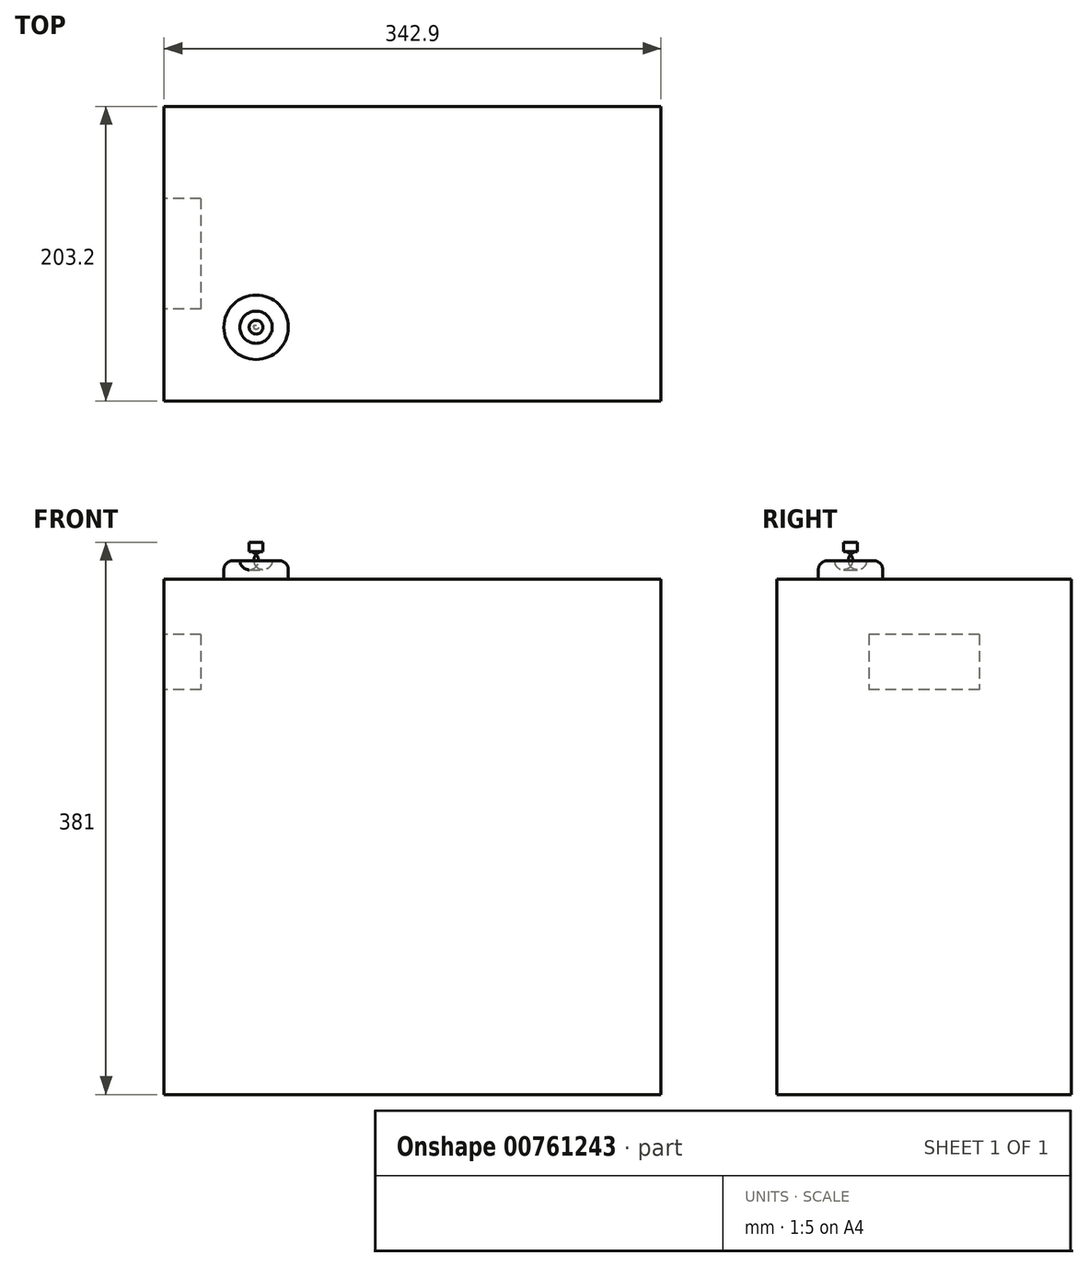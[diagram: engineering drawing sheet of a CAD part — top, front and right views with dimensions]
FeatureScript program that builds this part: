
annotation { "Feature Type Name" : "Feature", "Feature Type Description" : "" }
export const myFeature = defineFeature(function(context is Context, id is Id, definition is map)
    precondition{}
    {
        {
            var Q0;
            Q0=qCreatedBy(makeId("Top.planeOp"),FACE);
            var sketch = newSketch(context, id + "F0", { "sketchPlane" : qUnion([Q0])});
            skLineSegment(sketch, "E0.bottom", {"start": v(0, 203.2) * mm, "end": v(342.9, 203.2) * mm});
            skLineSegment(sketch, "E0.top", {"start": v(0, 0) * mm, "end": v(342.9, 0) * mm});
            skLineSegment(sketch, "E0.left", {"start": v(0, 203.2) * mm, "end": v(0, 0) * mm});
            skLineSegment(sketch, "E0.right", {"start": v(342.9, 203.2) * mm, "end": v(342.9, 0) * mm});
            skSolve(sketch);
        }
        {
            var Q0;
            Q0 = qSketchRegion(id + "F0", true);
            extrude(context, id + "F1", {"entities" : qUnion([Q0]), "depth" : 355.6 * mm, "offsetDistance" : 25 * mm});
        }
        {
            var Q0;
            Q0=makeQuery(id+"F1.opExtrude","SWEPT_FACE",FACE,{"disambiguationData":[OSD([sQuery(id+"F0.wireOp",EDGE,"E0.top")])]});
            cPlane(context, id + "F2", {"entities" : qUnion([Q0]), "cplaneType" : CPlaneType.OFFSET, "offset" : 50.8 * mm, "oppositeDirection" : true, "width" : 150 * mm, "height" : 150 * mm});
        }
        {
            var Q0;
            Q0=qCreatedBy(id+"F2.planeOp",FACE);
            var sketch = newSketch(context, id + "F3", { "sketchPlane" : qUnion([Q0])});
            skLineSegment(sketch, "E1", {"start": v(63.5, 323.9) * mm, "end": v(63.5, 400.93) * mm, "construction": true});
            skLineSegment(sketch, "E2", {"start": v(63.5, 355.6) * mm, "end": v(85.72, 355.6) * mm});
            skLineSegment(sketch, "E3", {"start": v(85.72, 355.6) * mm, "end": v(85.72, 361.95) * mm});
            skArc(sketch, "E4", {"start": v(85.72, 361.95) * mm, "mid": v(83.87, 366.44) * mm, "end": v(79.38, 368.3) * mm});
            skLineSegment(sketch, "E5", {"start": v(79.38, 368.3) * mm, "end": v(74.61, 368.3) * mm});
            skLineSegment(sketch, "E6", {"start": v(63.5, 381) * mm, "end": v(63.5, 355.6) * mm});
            skArc(sketch, "E7", {"start": v(74.61, 368.3) * mm, "mid": v(72.75, 372.8) * mm, "end": v(68.26, 374.65) * mm});
            skLineSegment(sketch, "E8", {"start": v(68.26, 374.65) * mm, "end": v(68.26, 381) * mm});
            skLineSegment(sketch, "E9", {"start": v(68.26, 381) * mm, "end": v(63.5, 381) * mm});
            skSolve(sketch);
        }
        {
            var Q0;
            Q0 = qSketchRegion(id + "F3", true);
            var Q1;
            Q1=sQuery(id+"F3.wireOp",EDGE,"E1");
            revolve(context, id + "F4", {"operationType" : NewBodyOperationType.ADD, "surfaceOperationType" : NewSurfaceOperationType.NEW, "entities" : qUnion([Q0]), "axis" : qUnion([Q1]), "revolveType" : RevolveType.FULL});
        }
        {
            var Q0;
            Q0=makeQuery(id+"F1.opExtrude","CAP_EDGE",EDGE,{"disambiguationData":[OSD([sQuery(id+"F0.wireOp",EDGE,"E0.top")])],"isStart":false});
            cPlane(context, id + "F5", {"entities" : qUnion([Q0]), "cplaneType" : CPlaneType.MID_PLANE, "offset" : 25 * mm, "width" : 150 * mm, "height" : 150 * mm});
        }
        {
            var Q0;
            Q0=makeQuery(id+"F1.opExtrude","SWEPT_FACE",FACE,{"disambiguationData":[OSD([sQuery(id+"F0.wireOp",EDGE,"E0.left")])]});
            var sketch = newSketch(context, id + "F6", { "sketchPlane" : qUnion([Q0])});
            skLineSegment(sketch, "E10.bottom", {"start": v(-139.7, 317.5) * mm, "end": v(-63.5, 317.5) * mm});
            skLineSegment(sketch, "E10.top", {"start": v(-139.7, 279.4) * mm, "end": v(-63.5, 279.4) * mm});
            skLineSegment(sketch, "E10.left", {"start": v(-139.7, 317.5) * mm, "end": v(-139.7, 279.4) * mm});
            skLineSegment(sketch, "E10.right", {"start": v(-63.5, 317.5) * mm, "end": v(-63.5, 279.4) * mm});
            skSolve(sketch);
        }
        {
            var Q0;
            Q0 = qSketchRegion(id + "F6", true);
            extrude(context, id + "F7", {"entities" : qUnion([Q0]), "operationType" : NewBodyOperationType.REMOVE, "oppositeDirection" : true, "depth" : 25.4 * mm, "offsetDistance" : 25 * mm});
        }
    });
